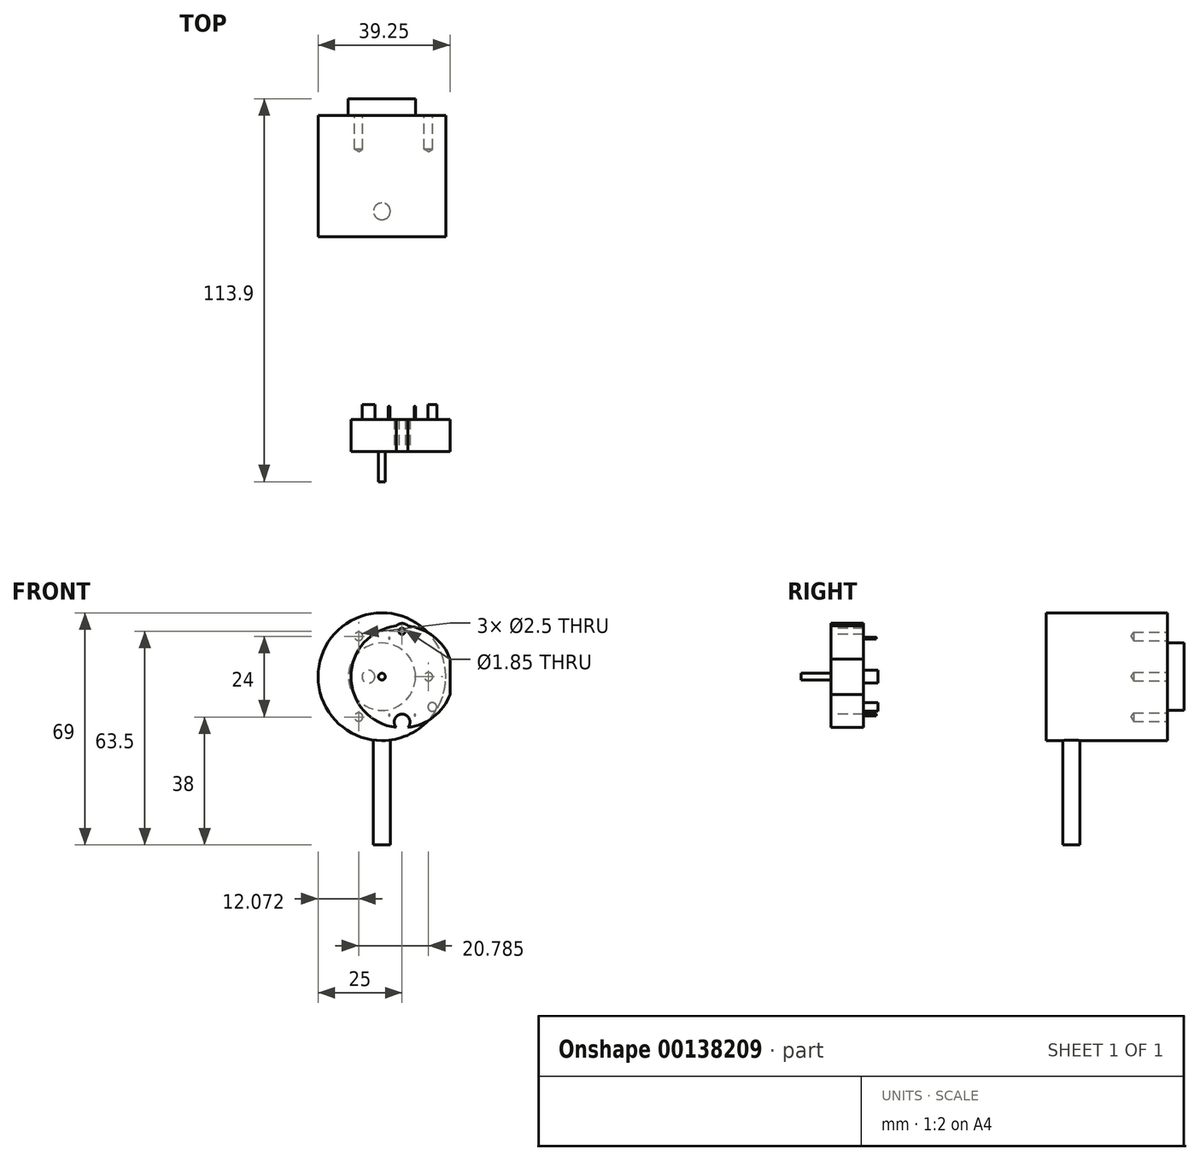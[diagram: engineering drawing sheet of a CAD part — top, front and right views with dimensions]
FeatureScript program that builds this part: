
annotation { "Feature Type Name" : "Feature", "Feature Type Description" : "" }
export const myFeature = defineFeature(function(context is Context, id is Id, definition is map)
    precondition{}
    {
        {
            var Q0;
            Q0=qCreatedBy(makeId("Front.planeOp"),FACE);
            cPlane(context, id + "F0", {"entities" : qUnion([Q0]), "cplaneType" : CPlaneType.OFFSET, "offset" : 100 * mm, "oppositeDirection" : true, "width" : 152.4 * mm, "height" : 152.4 * mm});
        }
        {
            var Q0;
            Q0=qCreatedBy(id+"F0.planeOp",FACE);
            var sketch = newSketch(context, id + "F1", { "sketchPlane" : qUnion([Q0])});
            skPoint(sketch, "E0.0", {"position": v(0, 0) * mm});
            skCircle(sketch, "E1", {"center": v(0, 0) * mm, "radius": 19 * mm});
            skSolve(sketch);
        }
        {
            var Q0;
            Q0=makeQuery(id+"F1.imprint","IMPRINT",FACE,{"disambiguationData":[TD([[makeQuery(id+"F1.imprint","IMPRINT",EDGE,{"derivedFrom":sQuery(id+"F1.wireOp",EDGE,"E1")}),1.0]])]});
            extrude(context, id + "F2", {"entities" : qUnion([Q0]), "depth" : 36 * mm});
        }
        {
            var Q0;
            Q0=makeQuery(id+"F2.opExtrude","CAP_FACE",FACE,{"disambiguationData":[OSD([sQuery(id+"F1.wireOp",EDGE,"E1")])],"isStart":true});
            var sketch = newSketch(context, id + "F3", { "sketchPlane" : qUnion([Q0])});
            skPoint(sketch, "E2.0", {"position": v(0, 0) * mm});
            skCircle(sketch, "E3", {"center": v(0, 0) * mm, "radius": 10 * mm});
            skPoint(sketch, "E4", {"position": v(-13.86, 0) * mm});
            skPoint(sketch, "E5.1.0", {"position": v(6.93, -12) * mm});
            skPoint(sketch, "E5.2.0", {"position": v(6.93, 12) * mm});
            skSolve(sketch);
        }
        {
            var Q0;
            Q0=makeQuery(id+"F3.imprint","IMPRINT",FACE,{"disambiguationData":[TD([[makeQuery(id+"F3.imprint","IMPRINT",EDGE,{"derivedFrom":sQuery(id+"F3.wireOp",EDGE,"E3")}),1.0]])]});
            extrude(context, id + "F4", {"entities" : qUnion([Q0]), "operationType" : NewBodyOperationType.ADD, "depth" : 5 * mm});
        }
        {
            var Q0;
            Q0=sQuery(id+"F3.wireOp",VERTEX,"E4");
            var Q1;
            Q1=sQuery(id+"F3.wireOp",VERTEX,"E5.1.0");
            var Q2;
            Q2=sQuery(id+"F3.wireOp",VERTEX,"E5.2.0");
            var Q3;
            Q3=makeQuery(id+"F2.opExtrude","SWEPT_BODY",BODY,{"disambiguationData":[OSD([sQuery(id+"F1.wireOp",EDGE,"E1")])]});
            hole(context, id + "F5", {"style" : HoleStyle.SIMPLE, "endStyle" : HoleEndStyle.BLIND, "holeDiameter" : 2.5 * mm, "holeDepth" : 10 * mm, "locations" : qUnion([Q0, Q1, Q2]), "scope" : qUnion([Q3])});
        }
        {
            var Q0;
            Q0=qCreatedBy(makeId("Top.planeOp"),FACE);
            var sketch = newSketch(context, id + "F6", { "sketchPlane" : qUnion([Q0])});
            skLineSegment(sketch, "E6", {"start": v(19, 100) * mm, "end": v(19, 64) * mm});
            skLineSegment(sketch, "E7", {"start": v(-19, 64) * mm, "end": v(-19, 100) * mm});
            skPoint(sketch, "E8.0", {"position": v(0, 0) * mm});
            skCircle(sketch, "E9", {"center": v(0, 71.5) * mm, "radius": 2.5 * mm});
            skSolve(sketch);
        }
        {
            var Q0;
            Q0=makeQuery(id+"F6.imprint","IMPRINT",FACE,{"disambiguationData":[TD([[makeQuery(id+"F6.imprint","IMPRINT",EDGE,{"derivedFrom":sQuery(id+"F6.wireOp",EDGE,"E9")}),1.0]])]});
            extrude(context, id + "F7", {"entities" : qUnion([Q0]), "operationType" : NewBodyOperationType.ADD, "oppositeDirection" : true, "depth" : 50 * mm});
        }
        {
            var Q0;
            Q0=qCreatedBy(makeId("Front.planeOp"),FACE);
            var sketch = newSketch(context, id + "F8", { "sketchPlane" : qUnion([Q0])});
            skCircle(sketch, "E10", {"center": v(6, 0) * mm, "radius": 15.2 * mm});
            skLineSegment(sketch, "E11", {"start": v(20.25, 5.29) * mm, "end": v(20.25, -5.29) * mm});
            skCircle(sketch, "E12", {"center": v(6, 13.5) * mm, "radius": 2.35 * mm});
            skLineSegment(sketch, "E13", {"start": v(-31.9, 0) * mm, "end": v(33.8, 0) * mm, "construction": true});
            skCircle(sketch, "E14.MirrorC", {"center": v(6, -13.5) * mm, "radius": 2.35 * mm});
            skCircle(sketch, "E15", {"center": v(0, 0) * mm, "radius": 1 * mm});
            skCircle(sketch, "E16", {"center": v(6, 13.5) * mm, "radius": 0.93 * mm});
            skCircle(sketch, "E17.MirrorC", {"center": v(6, -13.5) * mm, "radius": 0.93 * mm});
            skSolve(sketch);
        }
        {
            var Q0;
            {var subQ0=sQuery(id+"F8.wireOp",EDGE,"E11");Q0=makeQuery(id+"F8.imprint","IMPRINT",FACE,{"disambiguationData":[TD([[makeQuery(id+"F8.imprint","IMPRINT",EDGE,{"derivedFrom":subQ0}),-1.0]])]});}
            var Q1;
            {var subQ0=sQuery(id+"F8.wireOp",EDGE,"E12");var subQ1=sQuery(id+"F8.wireOp",EDGE,"E10");var subQ2=makeQuery(id+"F8.imprint","INTERSECT",VERTEX,{"disambiguationData":[OD(0.0)],"derivedFrom":[subQ1,subQ0]});Q1=makeQuery(id+"F8.imprint","IMPRINT",FACE,{"disambiguationData":[TD([[makeQuery(id+"F8.imprint","IMPRINT",EDGE,{"disambiguationData":[TD([[subQ2,-1.0]])],"derivedFrom":subQ1}),-1.0]])]});}
            var Q2;
            {var subQ0=sQuery(id+"F8.wireOp",EDGE,"E12");var subQ1=sQuery(id+"F8.wireOp",EDGE,"E10");var subQ2=makeQuery(id+"F8.imprint","INTERSECT",VERTEX,{"disambiguationData":[OD(0.0)],"derivedFrom":[subQ1,subQ0]});Q2=makeQuery(id+"F8.imprint","IMPRINT",FACE,{"disambiguationData":[TD([[makeQuery(id+"F8.imprint","IMPRINT",EDGE,{"disambiguationData":[TD([[subQ2,-1.0]])],"derivedFrom":subQ1}),1.0]])]});}
            var Q3;
            {var subQ0=sQuery(id+"F8.wireOp",EDGE,"E14.MirrorC");var subQ1=sQuery(id+"F8.wireOp",EDGE,"E10");var subQ2=makeQuery(id+"F8.imprint","INTERSECT",VERTEX,{"disambiguationData":[OD(0.0)],"derivedFrom":[subQ1,subQ0]});Q3=makeQuery(id+"F8.imprint","IMPRINT",FACE,{"disambiguationData":[TD([[makeQuery(id+"F8.imprint","IMPRINT",EDGE,{"disambiguationData":[TD([[subQ2,-1.0]])],"derivedFrom":subQ1}),1.0]])]});}
            var Q4;
            {var subQ0=sQuery(id+"F8.wireOp",EDGE,"E14.MirrorC");var subQ1=sQuery(id+"F8.wireOp",EDGE,"E10");var subQ2=makeQuery(id+"F8.imprint","INTERSECT",VERTEX,{"disambiguationData":[OD(0.0)],"derivedFrom":[subQ1,subQ0]});Q4=makeQuery(id+"F8.imprint","IMPRINT",FACE,{"disambiguationData":[TD([[makeQuery(id+"F8.imprint","IMPRINT",EDGE,{"disambiguationData":[TD([[subQ2,-1.0]])],"derivedFrom":subQ1}),-1.0]])]});}
            var Q5;
            Q5=makeQuery(id+"F8.imprint","IMPRINT",FACE,{"disambiguationData":[TD([[makeQuery(id+"F8.imprint","IMPRINT",EDGE,{"derivedFrom":sQuery(id+"F8.wireOp",EDGE,"E15")}),1.0]])]});
            extrude(context, id + "F9", {"entities" : qUnion([Q0, Q1, Q2, Q3, Q4, Q5]), "oppositeDirection" : true, "depth" : 9.6 * mm});
        }
        {
            var Q0;
            Q0=makeQuery(id+"F8.imprint","IMPRINT",FACE,{"disambiguationData":[TD([[makeQuery(id+"F8.imprint","IMPRINT",EDGE,{"derivedFrom":sQuery(id+"F8.wireOp",EDGE,"E15")}),1.0]])]});
            extrude(context, id + "F10", {"entities" : qUnion([Q0]), "operationType" : NewBodyOperationType.ADD, "depth" : 8.9 * mm});
        }
        {
            var Q0;
            Q0=makeQuery(id+"F9.opExtrude","CAP_FACE",FACE,{"disambiguationData":[OSD([sQuery(id+"F8.wireOp",EDGE,"E10"),sQuery(id+"F8.wireOp",EDGE,"E11"),sQuery(id+"F8.wireOp",EDGE,"E12"),sQuery(id+"F8.wireOp",EDGE,"E14.MirrorC")])],"isStart":false});
            var sketch = newSketch(context, id + "F11", { "sketchPlane" : qUnion([Q0])});
            skPoint(sketch, "E18.0", {"position": v(0, 0) * mm});
            skCircle(sketch, "E19", {"center": v(4, 0) * mm, "radius": 1.9 * mm});
            skPoint(sketch, "E20.0", {"position": v(-6, -13.5) * mm});
            skPoint(sketch, "E21.0", {"position": v(-6, 13.5) * mm});
            skLineSegment(sketch, "E22", {"start": v(-6, -13.5) * mm, "end": v(-6, 13.5) * mm, "construction": true});
            skCircle(sketch, "E23", {"center": v(-15, -9) * mm, "radius": 1.3 * mm});
            skLineSegment(sketch, "E24", {"start": v(-15, -9) * mm, "end": v(4, 0) * mm, "construction": true});
            skCircle(sketch, "E25", {"center": v(-9.8, 11.43) * mm, "radius": 0.25 * mm});
            skCircle(sketch, "E26.0.1.0", {"center": v(-9.8, -11.43) * mm, "radius": 0.25 * mm});
            skCircle(sketch, "E26.1.0.0", {"center": v(-2.2, 11.43) * mm, "radius": 0.25 * mm});
            skCircle(sketch, "E26.1.1.0", {"center": v(-2.2, -11.43) * mm, "radius": 0.25 * mm});
            skLineSegment(sketch, "E26.direction1", {"start": v(-9.8, 11.43) * mm, "end": v(-2.2, 11.43) * mm, "construction": true});
            skLineSegment(sketch, "E26.direction2", {"start": v(-9.8, 11.43) * mm, "end": v(-9.8, -11.43) * mm, "construction": true});
            skLineSegment(sketch, "E27", {"start": v(-25.73, 0) * mm, "end": v(15.3, 0) * mm, "construction": true});
            skSolve(sketch);
        }
        {
            var Q0;
            Q0=makeQuery(id+"F11.imprint","IMPRINT",FACE,{"disambiguationData":[TD([[makeQuery(id+"F11.imprint","IMPRINT",EDGE,{"derivedFrom":sQuery(id+"F11.wireOp",EDGE,"E19")}),1.0]])]});
            var Q1;
            Q1=makeQuery(id+"F11.imprint","IMPRINT",FACE,{"disambiguationData":[TD([[makeQuery(id+"F11.imprint","IMPRINT",EDGE,{"derivedFrom":sQuery(id+"F11.wireOp",EDGE,"E23")}),1.0]])]});
            extrude(context, id + "F12", {"entities" : qUnion([Q0, Q1]), "operationType" : NewBodyOperationType.ADD, "depth" : 4.4 * mm});
        }
        {
            var Q0;
            Q0=makeQuery(id+"F11.imprint","IMPRINT",FACE,{"disambiguationData":[TD([[makeQuery(id+"F11.imprint","IMPRINT",EDGE,{"derivedFrom":sQuery(id+"F11.wireOp",EDGE,"E25")}),1.0]])]});
            var Q1;
            Q1=makeQuery(id+"F11.imprint","IMPRINT",FACE,{"disambiguationData":[TD([[makeQuery(id+"F11.imprint","IMPRINT",EDGE,{"derivedFrom":sQuery(id+"F11.wireOp",EDGE,"E26.1.0.0")}),1.0]])]});
            var Q2;
            Q2=makeQuery(id+"F11.imprint","IMPRINT",FACE,{"disambiguationData":[TD([[makeQuery(id+"F11.imprint","IMPRINT",EDGE,{"derivedFrom":sQuery(id+"F11.wireOp",EDGE,"E26.1.1.0")}),1.0]])]});
            var Q3;
            Q3=makeQuery(id+"F11.imprint","IMPRINT",FACE,{"disambiguationData":[TD([[makeQuery(id+"F11.imprint","IMPRINT",EDGE,{"derivedFrom":sQuery(id+"F11.wireOp",EDGE,"E26.0.1.0")}),1.0]])]});
            extrude(context, id + "F13", {"entities" : qUnion([Q0, Q1, Q2, Q3]), "operationType" : NewBodyOperationType.ADD, "depth" : 3.9 * mm});
        }
        {
            var Q0;
            Q0=qCreatedBy(makeId("Front.planeOp"), FACE);
            cPlane(context, id + "F14", {"entities" : qUnion([Q0]), "cplaneType" : CPlaneType.OFFSET, "offset" : 1 * mm, "width" : 150 * mm, "height" : 150 * mm});
        }
    });
